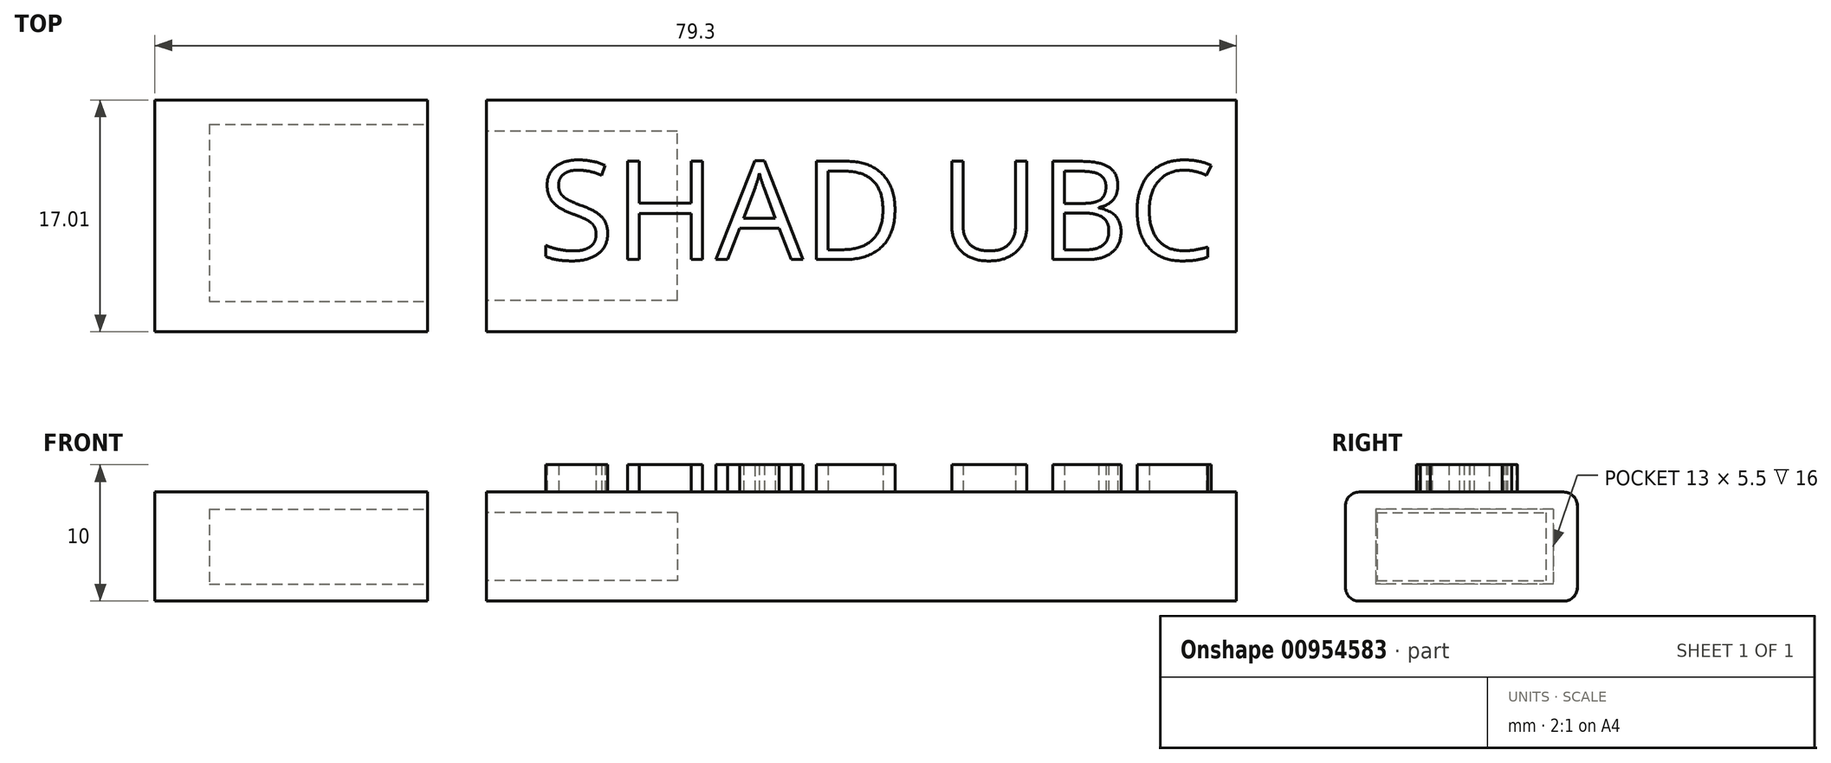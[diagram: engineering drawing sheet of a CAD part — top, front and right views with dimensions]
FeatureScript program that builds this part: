
annotation { "Feature Type Name" : "Feature", "Feature Type Description" : "" }
export const myFeature = defineFeature(function(context is Context, id is Id, definition is map)
    precondition{}
    {
        {
            var Q0;
            Q0=qCreatedBy(makeId("Front.planeOp"),FACE);
            var sketch = newSketch(context, id + "F0", { "sketchPlane" : qUnion([Q0])});
            skLineSegment(sketch, "E0.bottom", {"start": v(7.5, 4) * mm, "end": v(-7.5, 4) * mm});
            skLineSegment(sketch, "E0.top", {"start": v(7.5, -4) * mm, "end": v(-7.5, -4) * mm});
            skLineSegment(sketch, "E0.left", {"start": v(8.5, 3) * mm, "end": v(8.5, -3) * mm});
            skLineSegment(sketch, "E0.right", {"start": v(-8.5, 3) * mm, "end": v(-8.5, -3) * mm});
            skPoint(sketch, "E0.middle", {"position": v(0, 0) * mm});
            skPoint(sketch, "E1.visualSharp", {"position": v(-8.5, -4) * mm});
            skArc(sketch, "E1.filletArc", {"start": v(-8.5, -3) * mm, "mid": v(-8.2, -3.7) * mm, "end": v(-7.5, -4) * mm});
            skPoint(sketch, "E2.visualSharp", {"position": v(8.5, -4) * mm});
            skArc(sketch, "E2.filletArc", {"start": v(7.5, -4) * mm, "mid": v(8.2, -3.7) * mm, "end": v(8.5, -3) * mm});
            skPoint(sketch, "E3.visualSharp", {"position": v(8.5, 4) * mm});
            skArc(sketch, "E3.filletArc", {"start": v(8.5, 3) * mm, "mid": v(8.2, 3.7) * mm, "end": v(7.5, 4) * mm});
            skPoint(sketch, "E4.visualSharp", {"position": v(-8.5, 4) * mm});
            skArc(sketch, "E4.filletArc", {"start": v(-7.5, 4) * mm, "mid": v(-8.2, 3.7) * mm, "end": v(-8.5, 3) * mm});
            skSolve(sketch);
        }
        {
            var Q0;
            Q0 = qSketchRegion(id + "F0", true);
            extrude(context, id + "F1", {"entities" : qUnion([Q0]), "depth" : 55 * mm, "offsetDistance" : 25 * mm});
        }
        {
            var Q0;
            Q0=makeQuery(id+"F1.opExtrude","SWEPT_BODY",BODY,{"disambiguationData":[OSD([sQuery(id+"F0.wireOp",EDGE,"E0.bottom"),sQuery(id+"F0.wireOp",EDGE,"E0.top"),sQuery(id+"F0.wireOp",EDGE,"E0.left"),sQuery(id+"F0.wireOp",EDGE,"E0.right"),sQuery(id+"F0.wireOp",EDGE,"E1.filletArc"),sQuery(id+"F0.wireOp",EDGE,"E2.filletArc"),sQuery(id+"F0.wireOp",EDGE,"E3.filletArc"),sQuery(id+"F0.wireOp",EDGE,"E4.filletArc")])]});
            transform(context, id + "F2", {"entities" : qUnion([Q0]), "transformType" : TransformType.TRANSLATION_3D, "dx" : 0 * mm, "dy" : 27.4 * mm, "dz" : 0 * mm, "makeCopy" : false});
        }
        {
            var Q0;
            Q0=makeQuery(id+"F1.opExtrude","CAP_FACE",FACE,{"disambiguationData":[OSD([sQuery(id+"F0.wireOp",EDGE,"E0.bottom"),sQuery(id+"F0.wireOp",EDGE,"E0.top"),sQuery(id+"F0.wireOp",EDGE,"E0.left"),sQuery(id+"F0.wireOp",EDGE,"E0.right"),sQuery(id+"F0.wireOp",EDGE,"E1.filletArc"),sQuery(id+"F0.wireOp",EDGE,"E2.filletArc"),sQuery(id+"F0.wireOp",EDGE,"E3.filletArc"),sQuery(id+"F0.wireOp",EDGE,"E4.filletArc")])],"isStart":false});
            var sketch = newSketch(context, id + "F3", { "sketchPlane" : qUnion([Q0])});
            skLineSegment(sketch, "E5.bottom", {"start": v(6.2, 2.5) * mm, "end": v(-6.2, 2.5) * mm});
            skLineSegment(sketch, "E5.top", {"start": v(6.2, -2.5) * mm, "end": v(-6.2, -2.5) * mm});
            skLineSegment(sketch, "E5.left", {"start": v(6.2, 2.5) * mm, "end": v(6.2, -2.5) * mm});
            skLineSegment(sketch, "E5.right", {"start": v(-6.2, 2.5) * mm, "end": v(-6.2, -2.5) * mm});
            skPoint(sketch, "E5.middle", {"position": v(0, 0) * mm});
            skSolve(sketch);
        }
        {
            var Q0;
            Q0 = qSketchRegion(id + "F3", true);
            extrude(context, id + "F4", {"entities" : qUnion([Q0]), "operationType" : NewBodyOperationType.REMOVE, "oppositeDirection" : true, "depth" : 14 * mm, "offsetDistance" : 25 * mm});
        }
        {
            var Q0;
            Q0=makeQuery(id+"F1.opExtrude","SWEPT_FACE",FACE,{"disambiguationData":[OSD([sQuery(id+"F0.wireOp",EDGE,"E0.bottom")])]});
            var sketch = newSketch(context, id + "F5", { "sketchPlane" : qUnion([Q0])});
            skText(sketch, "E6", { "text": "SHAD UBC", "fontName": "OpenSans-Regular.ttf"});
            const initialGuessF5  = {"E6": [-0.02196, -0.0054, 1, 0, 0.00727]};
            skSetInitialGuess(sketch, initialGuessF5);
            skSolve(sketch);
        }
        {
            var Q0;
            Q0=makeQuery(id+"F1.opExtrude","SWEPT_BODY",BODY,{"disambiguationData":[OSD([sQuery(id+"F0.wireOp",EDGE,"E0.bottom"),sQuery(id+"F0.wireOp",EDGE,"E0.top"),sQuery(id+"F0.wireOp",EDGE,"E0.left"),sQuery(id+"F0.wireOp",EDGE,"E0.right"),sQuery(id+"F0.wireOp",EDGE,"E1.filletArc"),sQuery(id+"F0.wireOp",EDGE,"E2.filletArc"),sQuery(id+"F0.wireOp",EDGE,"E3.filletArc"),sQuery(id+"F0.wireOp",EDGE,"E4.filletArc")])]});
            var Q1;
            Q1=makeQuery(id+"F1.opExtrude","CAP_EDGE",EDGE,{"disambiguationData":[OSD([sQuery(id+"F0.wireOp",EDGE,"E0.right")])],"isStart":true});
            transform(context, id + "F6", {"entities" : qUnion([Q0]), "transformType" : TransformType.ROTATION, "transformAxis" : qUnion([Q1]), "angle" : 90 * degree, "makeCopy" : false});
        }
        {
            var Q0;
            Q0=makeQuery(id+"F1.opExtrude","SWEPT_BODY",BODY,{"disambiguationData":[OSD([sQuery(id+"F0.wireOp",EDGE,"E0.bottom"),sQuery(id+"F0.wireOp",EDGE,"E0.top"),sQuery(id+"F0.wireOp",EDGE,"E0.left"),sQuery(id+"F0.wireOp",EDGE,"E0.right"),sQuery(id+"F0.wireOp",EDGE,"E1.filletArc"),sQuery(id+"F0.wireOp",EDGE,"E2.filletArc"),sQuery(id+"F0.wireOp",EDGE,"E3.filletArc"),sQuery(id+"F0.wireOp",EDGE,"E4.filletArc")])]});
            transform(context, id + "F7", {"entities" : qUnion([Q0]), "transformType" : TransformType.TRANSLATION_3D, "dx" : 37.7 * mm, "dy" : -21.1 * mm, "dz" : 0 * mm, "makeCopy" : false});
        }
        {
            var Q0;
            Q0 = qSketchRegion(id + "F5", true);
            extrude(context, id + "F8", {"entities" : qUnion([Q0]), "operationType" : NewBodyOperationType.ADD, "depth" : 2 * mm, "offsetDistance" : 25 * mm});
        }
        {
            var Q0;
            Q0=qCreatedBy(makeId("Right.planeOp"),FACE);
            var sketch = newSketch(context, id + "F9", { "sketchPlane" : qUnion([Q0])});
            skLineSegment(sketch, "E7.bottom", {"start": v(-28.53, 8) * mm, "end": v(-13.53, 8) * mm});
            skLineSegment(sketch, "E7.top", {"start": v(-28.53, 0) * mm, "end": v(-13.53, 0) * mm});
            skLineSegment(sketch, "E7.left", {"start": v(-29.53, 7) * mm, "end": v(-29.53, 1) * mm});
            skLineSegment(sketch, "E7.right", {"start": v(-12.53, 7) * mm, "end": v(-12.53, 1) * mm});
            skPoint(sketch, "E8.visualSharp", {"position": v(-29.53, 8) * mm});
            skArc(sketch, "E8.filletArc", {"start": v(-28.53, 8) * mm, "mid": v(-29.24, 7.7) * mm, "end": v(-29.53, 7) * mm});
            skPoint(sketch, "E9.visualSharp", {"position": v(-12.53, 8) * mm});
            skArc(sketch, "E9.filletArc", {"start": v(-12.53, 7) * mm, "mid": v(-12.82, 7.7) * mm, "end": v(-13.53, 8) * mm});
            skPoint(sketch, "E10.visualSharp", {"position": v(-12.53, 0) * mm});
            skArc(sketch, "E10.filletArc", {"start": v(-13.53, 0) * mm, "mid": v(-12.82, 0.3) * mm, "end": v(-12.53, 1) * mm});
            skPoint(sketch, "E11.visualSharp", {"position": v(-29.53, 0) * mm});
            skArc(sketch, "E11.filletArc", {"start": v(-29.53, 1) * mm, "mid": v(-29.24, 0.3) * mm, "end": v(-28.53, 0) * mm});
            skSolve(sketch);
        }
        {
            var Q0;
            Q0=makeQuery(id+"F9.imprint","IMPRINT",FACE,{"disambiguationData":[TD([[makeQuery(id+"F9.imprint","IMPRINT",EDGE,{"derivedFrom":sQuery(id+"F9.wireOp",EDGE,"E7.bottom")}),-1.0]])]});
            extrude(context, id + "F10", {"entities" : qUnion([Q0]), "depth" : 20 * mm, "offsetDistance" : 25 * mm});
        }
        {
            var Q0;
            Q0=makeQuery(id+"F10.opExtrude","SWEPT_BODY",BODY,{"disambiguationData":[OSD([sQuery(id+"F9.wireOp",EDGE,"E7.bottom"),sQuery(id+"F9.wireOp",EDGE,"E7.top"),sQuery(id+"F9.wireOp",EDGE,"E7.left"),sQuery(id+"F9.wireOp",EDGE,"E7.right"),sQuery(id+"F9.wireOp",EDGE,"E8.filletArc"),sQuery(id+"F9.wireOp",EDGE,"E9.filletArc"),sQuery(id+"F9.wireOp",EDGE,"E10.filletArc"),sQuery(id+"F9.wireOp",EDGE,"E11.filletArc")])]});
            transform(context, id + "F11", {"entities" : qUnion([Q0]), "transformType" : TransformType.TRANSLATION_3D, "dx" : -53.2 * mm, "dy" : 46.8 * mm, "dz" : -4 * mm, "makeCopy" : false});
        }
        {
            var Q0;
            Q0=makeQuery(id+"F10.opExtrude","SWEPT_BODY",BODY,{"disambiguationData":[OSD([sQuery(id+"F9.wireOp",EDGE,"E7.bottom"),sQuery(id+"F9.wireOp",EDGE,"E7.top"),sQuery(id+"F9.wireOp",EDGE,"E7.left"),sQuery(id+"F9.wireOp",EDGE,"E7.right"),sQuery(id+"F9.wireOp",EDGE,"E8.filletArc"),sQuery(id+"F9.wireOp",EDGE,"E9.filletArc"),sQuery(id+"F9.wireOp",EDGE,"E10.filletArc"),sQuery(id+"F9.wireOp",EDGE,"E11.filletArc")])]});
            transform(context, id + "F12", {"entities" : qUnion([Q0]), "transformType" : TransformType.TRANSLATION_3D, "dx" : 104 * mm, "dy" : -25.77 * mm, "dz" : 0 * mm, "makeCopy" : false});
        }
        {
            var Q0;
            Q0=makeQuery(id+"F10.opExtrude","CAP_FACE",FACE,{"disambiguationData":[OSD([sQuery(id+"F9.wireOp",EDGE,"E7.bottom"),sQuery(id+"F9.wireOp",EDGE,"E7.top"),sQuery(id+"F9.wireOp",EDGE,"E7.left"),sQuery(id+"F9.wireOp",EDGE,"E7.right"),sQuery(id+"F9.wireOp",EDGE,"E8.filletArc"),sQuery(id+"F9.wireOp",EDGE,"E9.filletArc"),sQuery(id+"F9.wireOp",EDGE,"E10.filletArc"),sQuery(id+"F9.wireOp",EDGE,"E11.filletArc")])],"isStart":false});
            var sketch = newSketch(context, id + "F13", { "sketchPlane" : qUnion([Q0])});
            skLineSegment(sketch, "E12.bottom", {"start": v(6.72, 2.75) * mm, "end": v(-6.28, 2.75) * mm});
            skLineSegment(sketch, "E12.top", {"start": v(6.72, -2.75) * mm, "end": v(-6.28, -2.75) * mm});
            skLineSegment(sketch, "E12.left", {"start": v(6.72, 2.75) * mm, "end": v(6.72, -2.75) * mm});
            skLineSegment(sketch, "E12.right", {"start": v(-6.28, 2.75) * mm, "end": v(-6.28, -2.75) * mm});
            skPoint(sketch, "E12.middle", {"position": v(0.22, 0) * mm});
            skSolve(sketch);
        }
        {
            var Q0;
            Q0=makeQuery(id+"F13.imprint","IMPRINT",FACE,{"disambiguationData":[TD([[makeQuery(id+"F13.imprint","IMPRINT",EDGE,{"derivedFrom":sQuery(id+"F13.wireOp",EDGE,"E12.bottom")}),1.0]])]});
            extrude(context, id + "F14", {"entities" : qUnion([Q0]), "operationType" : NewBodyOperationType.REMOVE, "oppositeDirection" : true, "depth" : 16 * mm, "offsetDistance" : 25 * mm});
        }
        {
            var Q0;
            Q0=makeQuery(id+"F10.opExtrude","SWEPT_BODY",BODY,{"disambiguationData":[OSD([sQuery(id+"F9.wireOp",EDGE,"E7.bottom"),sQuery(id+"F9.wireOp",EDGE,"E7.top"),sQuery(id+"F9.wireOp",EDGE,"E7.left"),sQuery(id+"F9.wireOp",EDGE,"E7.right"),sQuery(id+"F9.wireOp",EDGE,"E8.filletArc"),sQuery(id+"F9.wireOp",EDGE,"E9.filletArc"),sQuery(id+"F9.wireOp",EDGE,"E10.filletArc"),sQuery(id+"F9.wireOp",EDGE,"E11.filletArc")])]});
            transform(context, id + "F15", {"entities" : qUnion([Q0]), "transformType" : TransformType.TRANSLATION_3D, "dx" : -110 * mm, "dy" : 0 * mm, "dz" : 0 * mm, "makeCopy" : false});
        }
        {
            var Q0;
            Q0=makeQuery(id+"F1.opExtrude","SWEPT_BODY",BODY,{"disambiguationData":[OSD([sQuery(id+"F0.wireOp",EDGE,"E0.bottom"),sQuery(id+"F0.wireOp",EDGE,"E0.top"),sQuery(id+"F0.wireOp",EDGE,"E0.left"),sQuery(id+"F0.wireOp",EDGE,"E0.right"),sQuery(id+"F0.wireOp",EDGE,"E1.filletArc"),sQuery(id+"F0.wireOp",EDGE,"E2.filletArc"),sQuery(id+"F0.wireOp",EDGE,"E3.filletArc"),sQuery(id+"F0.wireOp",EDGE,"E4.filletArc")])]});
            transform(context, id + "F16", {"entities" : qUnion([Q0]), "transformType" : TransformType.TRANSLATION_3D, "dx" : 0 * mm, "dy" : 2.19 * mm, "dz" : 0 * mm, "makeCopy" : false});
        }
        {
            var Q0;
            Q0=makeQuery(id+"F10.opExtrude","SWEPT_BODY",BODY,{"disambiguationData":[OSD([sQuery(id+"F9.wireOp",EDGE,"E7.bottom"),sQuery(id+"F9.wireOp",EDGE,"E7.top"),sQuery(id+"F9.wireOp",EDGE,"E7.left"),sQuery(id+"F9.wireOp",EDGE,"E7.right"),sQuery(id+"F9.wireOp",EDGE,"E8.filletArc"),sQuery(id+"F9.wireOp",EDGE,"E9.filletArc"),sQuery(id+"F9.wireOp",EDGE,"E10.filletArc"),sQuery(id+"F9.wireOp",EDGE,"E11.filletArc")])]});
            transform(context, id + "F17", {"entities" : qUnion([Q0]), "transformType" : TransformType.TRANSLATION_3D, "dx" : 9.1 * mm, "dy" : 0 * mm, "dz" : 0 * mm, "makeCopy" : false});
        }
    });
